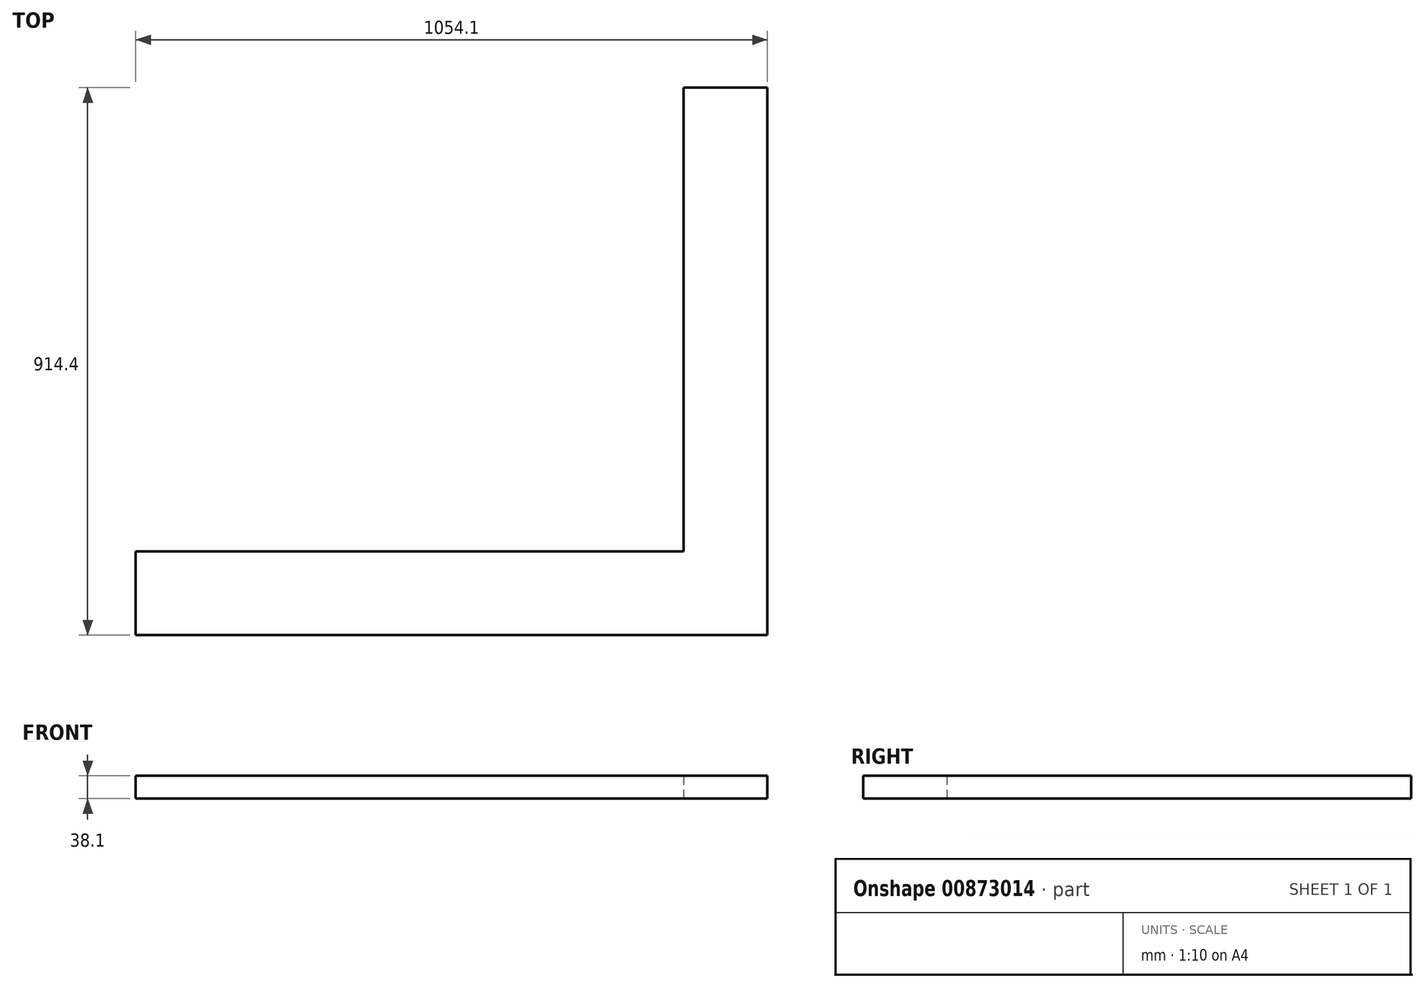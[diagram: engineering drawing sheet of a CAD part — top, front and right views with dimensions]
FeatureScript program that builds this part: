
annotation { "Feature Type Name" : "Feature", "Feature Type Description" : "" }
export const myFeature = defineFeature(function(context is Context, id is Id, definition is map)
    precondition{}
    {
        {
            var Q0;
            Q0=qCreatedBy(makeId("Top.planeOp"),FACE);
            var sketch = newSketch(context, id + "F0", { "sketchPlane" : qUnion([Q0])});
            skLineSegment(sketch, "E0.bottom", {"start": v(0, 0) * mm, "end": v(139.7, 0) * mm});
            skLineSegment(sketch, "E0.top", {"start": v(0, 914.4) * mm, "end": v(139.7, 914.4) * mm});
            skLineSegment(sketch, "E0.left", {"start": v(0, 0) * mm, "end": v(0, 914.4) * mm});
            skLineSegment(sketch, "E0.right", {"start": v(139.7, 0) * mm, "end": v(139.7, 914.4) * mm});
            skLineSegment(sketch, "E1.bottom", {"start": v(0, 0) * mm, "end": v(-914.4, 0) * mm});
            skLineSegment(sketch, "E1.top", {"start": v(0, 139.7) * mm, "end": v(-914.4, 139.7) * mm});
            skLineSegment(sketch, "E1.left", {"start": v(0, 0) * mm, "end": v(0, 139.7) * mm});
            skLineSegment(sketch, "E1.right", {"start": v(-914.4, 0) * mm, "end": v(-914.4, 139.7) * mm});
            skSolve(sketch);
        }
        {
            var Q0;
            Q0=makeQuery(id+"F0.imprint","IMPRINT",FACE,{"disambiguationData":[TD([[makeQuery(id+"F0.imprint","IMPRINT",EDGE,{"derivedFrom":sQuery(id+"F0.wireOp",EDGE,"E0.bottom")}),1.0]])]});
            var Q1;
            Q1=makeQuery(id+"F0.imprint","IMPRINT",FACE,{"disambiguationData":[TD([[makeQuery(id+"F0.imprint","IMPRINT",EDGE,{"derivedFrom":sQuery(id+"F0.wireOp",EDGE,"E1.bottom")}),-1.0]])]});
            extrude(context, id + "F1", {"entities" : qUnion([Q0, Q1]), "depth" : 38.1 * mm, "offsetDistance" : 25.4 * mm});
        }
    });
